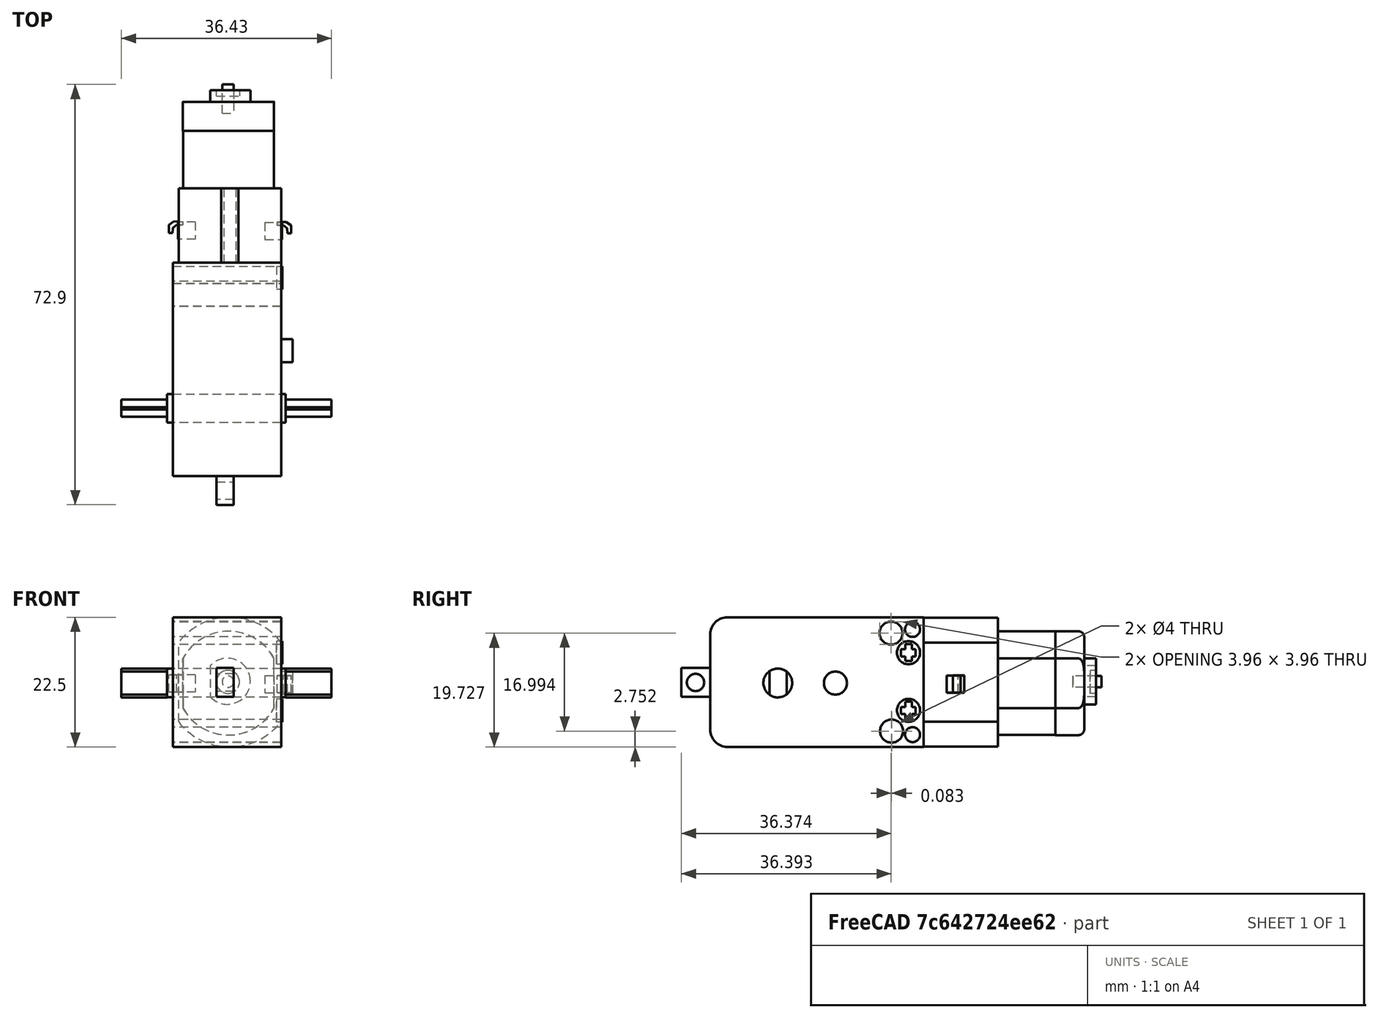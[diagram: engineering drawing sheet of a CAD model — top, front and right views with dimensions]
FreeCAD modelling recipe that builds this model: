
FCSTD DOCUMENT
Label: Motor
objects: Part::Part2DObjectPython×22, Part::Extrusion×22, Part::Cut×9, Part::Feature×4, Part::MultiCommon×3, Part::MultiFuse×3, Part::Fillet×2, App::DocumentObjectGroup×1
note: 65 computed .brp shape members not serialized (recipe doc carries the construction recipe); baked Part::Feature solids carry a one-line shape summary decoded from their .brp

FEATURE [Part::Part2DObjectPython] Circle  # Draft 2D object (typed FeaturePython)
  FirstAngle = 0
  LastAngle = 0
  Placement = pos=(9.4,37,11.25) rot=(0,0.707107,0.707107;3.14159rad)
  Radius = 11.25
FEATURE [Part::Extrusion] Extrude002  label="CaixaMotor"
  Base = -> Circle
  Dir = (0,13,0)
  Solid = false
FEATURE [Part::Part2DObjectPython] Rectangle004  # Draft 2D object (typed FeaturePython)
  FilletRadius = 0
  Height = -22.3491
  Length = 17.8
  Placement = pos=(0.516884,1.09014,22.3973) rot=(1,0,0;1.5708rad)
FEATURE [Part::Extrusion] Extrude008
  Base = -> Rectangle004
  Dir = (0,13,0)
  Placement = pos=(0,36,0) rot=(0,0,1;0rad)
  Solid = false
FEATURE [Part::Part2DObjectPython] Circle002  # Draft 2D object (typed FeaturePython)
  FirstAngle = 0
  LastAngle = 0
  Placement = pos=(59.8722,1.09014,36.5523) rot=(1,0,0;1.5708rad)
  Radius = 4
FEATURE [Part::Part2DObjectPython] Rectangle005  # Draft 2D object (typed FeaturePython)
  FilletRadius = 0
  Height = -8.04493
  Length = -5.41291
  Placement = pos=(56.9026,1.09014,40.4997) rot=(1,0,0;1.5708rad)
FEATURE [Part::Extrusion] Extrude009
  Base = -> Circle002
  Dir = (0,2,0)
  Solid = false
FEATURE [Part::Extrusion] Extrude010
  Base = -> Rectangle005
  Dir = (0,3,0)
  Placement = pos=(0,-0.5,0) rot=(0,0,1;0rad)
  Solid = false
FEATURE [Part::Fillet] Fillet
  Edges = 1 edges r=1: [Edge5]
FEATURE [Part::Part2DObjectPython] Rectangle006  # Draft 2D object (typed FeaturePython)
  FilletRadius = 0
  Height = 20.5
  Length = 15.8
  Placement = pos=(-34.3216,-16.9691,-15.1543) rot=(1,0,0;1.5708rad)
FEATURE [Part::Part2DObjectPython] Circle003  # Draft 2D object (typed FeaturePython)
  FirstAngle = 0
  LastAngle = 0
  Placement = pos=(-26.4216,-16.9691,-4.90432) rot=(1,0,0;1.5708rad)
  Radius = 9
FEATURE [Part::Extrusion] Extrude011
  Base = -> Rectangle006
  Dir = (0,10,0)
  Solid = false
FEATURE [Part::Extrusion] Extrude012
  Base = -> Circle003
  Dir = (0,10,0)
  Solid = false
FEATURE [Part::Part2DObjectPython] Rectangle007  # Draft 2D object (typed FeaturePython)
  FilletRadius = 0
  Height = 5
  Length = 5
  Placement = pos=(0,-19.0704,40.4297) rot=(0.57735,0.57735,0.57735;2.0944rad)
FEATURE [Part::Extrusion] Extrude013
  Base = -> Rectangle007
  Dir = (3,0,0)
  Solid = false
FEATURE [Part::Part2DObjectPython] Circle004  # Draft 2D object (typed FeaturePython)
  FirstAngle = 0
  LastAngle = 0
  Placement = pos=(3,-16.6188,42.8922) rot=(0.57735,0.57735,0.57735;2.0944rad)
  Radius = 1.5
FEATURE [Part::Extrusion] Extrude014
  Base = -> Circle004
  Dir = (5,0,0)
  Placement = pos=(-4,0,0) rot=(0,0,1;0rad)
  Solid = false
FEATURE [Part::Part2DObjectPython] Circle008  # Draft 2D object (typed FeaturePython)
  FirstAngle = 0
  LastAngle = 0
  Placement = pos=(9.57919,64.9001,11.2732) rot=(0,0.707107,0.707107;3.14159rad)
  Radius = 2
FEATURE [Part::Extrusion] Extrude015
  Base = -> Circle008
  Dir = (0,2,0)
  Placement = pos=(0,1,0) rot=(0,0,1;0rad)
  Solid = false
FEATURE [Part::Part2DObjectPython] Circle009  # Draft 2D object (typed FeaturePython)
  FirstAngle = 0
  LastAngle = 0
  Placement = pos=(9.57765,65.9001,11.232) rot=(0,0.707107,0.707107;3.14159rad)
  Radius = 1
FEATURE [Part::Part2DObjectPython] Circle010  # Draft 2D object (typed FeaturePython)
  FirstAngle = 0
  LastAngle = 0
  Placement = pos=(0,-28.9862,26.7464) rot=(0.57735,0.57735,0.57735;2.0944rad)
  Radius = 2
FEATURE [Part::Part2DObjectPython] Circle011  # Draft 2D object (typed FeaturePython)
  FirstAngle = 0
  LastAngle = 0
  Placement = pos=(0,-28.9045,14.2525) rot=(0.57735,0.57735,0.57735;2.0944rad)
  Radius = 2
FEATURE [Part::Extrusion] Extrude017
  Base = -> Circle010
  Dir = (25,0,0)
  Placement = pos=(-2.2,60.36,-7) rot=(0,0,1;0rad)
  Solid = false
FEATURE [Part::Extrusion] Extrude020
  Base = -> Circle011
  Dir = (25,0,0)
  Placement = pos=(-3.2,60.3616,-11.5) rot=(0,0,1;0rad)
  Solid = false
FEATURE [Part::Part2DObjectPython] Circle012  # Draft 2D object (typed FeaturePython)
  FirstAngle = 0
  LastAngle = 0
  Placement = pos=(0,-25.7698,21.2785) rot=(0.57735,0.57735,0.57735;2.0944rad)
  Radius = 1.3
FEATURE [Part::Extrusion] Extrude021
  Base = -> Circle012
  Dir = (25,0,0)
  Placement = pos=(-3.2,60.8663,-0.90035) rot=(0,0,1;0rad)
  Solid = false
FEATURE [Part::Feature] Extrude022
  Placement = pos=(-4.2,60.8663,-19.1548) rot=(0,0,1;0rad)
  shape: bbox 25 x 2.6 x 2.6 mm, 3 faces (baked)
FEATURE [Part::Cut] Cut003
  Tool = -> Extrude022
FEATURE [Part::Cut] Cut004
  Base = -> Cut003
  Tool = -> Extrude017
FEATURE [Part::Cut] Cut005
  Base = -> Cut004
  Tool = -> Extrude020
FEATURE [Part::Part2DObjectPython] DWire  # Draft 2D object (typed FeaturePython)
  Closed = true
  End = (24.1092,43.8585,0)
  FilletRadius = 0
  Start = (24.1092,43.8585,0)
FEATURE [Part::Extrusion] Extrude025
  Base = -> DWire
  Dir = (0,0,3)
  Placement = pos=(-6,0.17,9.39737) rot=(0,0,1;0rad)
  Solid = false
FEATURE [Part::Part2DObjectPython] Rectangle008  # Draft 2D object (typed FeaturePython)
  FilletRadius = 0
  Height = -3
  Length = 2.98
  Placement = pos=(22.53,42.0889,12.3974) rot=(0.57735,0.57735,0.57735;2.0944rad)
FEATURE [Part::Extrusion] Extrude026
  Base = -> Rectangle008
  Dir = (3,0,0)
  Placement = pos=(-6.56795,-1.09,0) rot=(0,0,1;0rad)
  Solid = false
FEATURE [Part::Part2DObjectPython] Circle013  # Draft 2D object (typed FeaturePython)
  FirstAngle = 0
  LastAngle = 0
  Placement = pos=(0,0,30) rot=(0.57735,0.57735,0.57735;2.0944rad)
  Radius = 2.5
FEATURE [Part::Extrusion] Extrude028
  Base = -> Circle013
  Dir = (36.6,0,0)
  Placement = pos=(-9.4,11.74,-20.9117) rot=(0,0,1;0rad)
  Solid = false
FEATURE [Part::Part2DObjectPython] Rectangle009  # Draft 2D object (typed FeaturePython)
  FilletRadius = 0
  Height = 5
  Length = 3
  Placement = pos=(0,0,-30) rot=(0.57735,0.57735,0.57735;2.0944rad)
FEATURE [Part::Extrusion] Extrude029
  Base = -> Rectangle009
  Dir = (8.9,0,0)
  Placement = pos=(-10.37,10.26,36.58) rot=(0,0,1;0rad)
  Solid = false
FEATURE [Part::MultiCommon] Common003
  Placement = pos=(29,0,2) rot=(0,0,1;0rad)
  Shapes = -> [Extrude028,Extrude029]
FEATURE [Part::Feature] Common004
  Placement = pos=(0.5,0,2) rot=(0,0,1;0rad)
  shape: bbox 7.93 x 3 x 4.992 mm, 8 faces (baked)
FEATURE [Part::Part2DObjectPython] Circle014  # Draft 2D object (typed FeaturePython)
  FirstAngle = 0
  LastAngle = 0
  Placement = pos=(18.8,11.7246,11.1008) rot=(0.57735,0.57735,0.57735;2.0944rad)
  Radius = 2.5
FEATURE [Part::Extrusion] Extrude030
  Base = -> Circle014
  Dir = (20.6,0,0)
  Placement = pos=(-19.8,0,0) rot=(0,0,1;0rad)
  Solid = false
FEATURE [Part::MultiFuse] Fusion002  label="EixoRoda0"
  Shapes = -> [Extrude030,Common004]
FEATURE [Part::Part2DObjectPython] Circle015  # Draft 2D object (typed FeaturePython)
  FirstAngle = 0
  LastAngle = 0
  Placement = pos=(18.8,21.72,11.075) rot=(0.57735,-0.57735,-0.57735;2.0944rad)
  Radius = 2
FEATURE [Part::Part2DObjectPython] Circle016  # Draft 2D object (typed FeaturePython)
  FirstAngle = 0
  LastAngle = 0
  Placement = pos=(0,-5.10148,33.3437) rot=(0.57735,0.57735,0.57735;2.0944rad)
  Radius = 2
FEATURE [Part::Extrusion] Extrude032
  Base = -> Circle016
  Dir = (1,0,0)
  Solid = false
FEATURE [Part::Part2DObjectPython] Rectangle010  # Draft 2D object (typed FeaturePython)
  FilletRadius = 0
  Height = -1.2407
  Length = 2.53364
  Placement = pos=(1,-6.39932,33.938) rot=(0.57735,0.57735,0.57735;2.0944rad)
FEATURE [Part::Part2DObjectPython] Rectangle011  # Draft 2D object (typed FeaturePython)
  FilletRadius = 0
  Height = -2.95156
  Length = 1.16234
  Placement = pos=(1,-5.6549,34.8391) rot=(0.57735,0.57735,0.57735;2.0944rad)
FEATURE [Part::Extrusion] Extrude033
  Base = -> Rectangle010
  Dir = (0.5,0,0)
  Placement = pos=(-0.2,0,0) rot=(0,0,1;0rad)
  Solid = false
FEATURE [Part::Extrusion] Extrude034
  Base = -> Rectangle011
  Dir = (0.5,0,0)
  Placement = pos=(-0.2,0,0) rot=(0,0,1;0rad)
  Solid = false
FEATURE [Part::Cut] Cut007
  Base = -> Extrude032
  Tool = -> Extrude033
FEATURE [Part::Feature] Part__Mirroring002  label="Alca2"
  Placement = pos=(-0.7,0.51,12.5) rot=(0,0,1;0rad)
  shape: bbox 4.572 x 3.074 x 3 mm, 16 faces (baked)
FEATURE [Part::Feature] Cut009  label="Parafuso002"
  Placement = pos=(18,39.5,-27) rot=(0,0,1;0rad)
  shape: bbox 1 x 4 x 4 mm, 20 faces (baked)
FEATURE [Part::Fillet] Fillet002  label="ParteMotor1"
  Base = -> Fillet
  Edges = 1 edges r=1: [Edge3]
  Placement = pos=(-0.226159,9.98502,-0.2) rot=(0,0,1;0rad)
FEATURE [Part::MultiCommon] Common  label="BooleanCaixaMotor"
  Placement = pos=(0.5,-0.1,0) rot=(0,0,1;0rad)
  Shapes = -> [Extrude008,Extrude002]
FEATURE [Part::Cut] Cut  label="SuporteEixo"
  Base = -> Extrude009
  Placement = pos=(-50.3996,63.81,-25.1656) rot=(0,0,1;0rad)
  Tool = -> Extrude010
FEATURE [Part::Cut] Cut002  label="ParteMotor2"
  Base = -> Cut
  Tool = -> Extrude015
FEATURE [Part::Extrusion] Extrude016  label="EixoMotor"
  Base = -> Circle009
  Dir = (0,5,0)
  Placement = pos=(-0.00220966,-3,0.0854275) rot=(0,0,1;0rad)
  Solid = false
FEATURE [Part::MultiCommon] Common002  label="CorpoMotor"
  Placement = pos=(36.1062,66.8259,15.9674) rot=(0,0,1;0rad)
  Shapes = -> [Extrude011,Extrude012]
FEATURE [Part::Cut] Cut001  label="Prendedor"
  Base = -> Extrude013
  Placement = pos=(7.59052,14.07,-31.7158) rot=(0,0,1;0rad)
  Tool = -> Extrude014
FEATURE [Part::Cut] Cut006  label="CaxiaFurada"
  Base = -> Cut005
  Tool = -> Extrude021
FEATURE [Part::MultiFuse] Fusion001  label="Alca1"
  Shapes = -> [Extrude025,Extrude026]
FEATURE [Part::MultiFuse] Fusion003  label="EixoRoda"
  Shapes = -> [Fusion002,Common003]
FEATURE [Part::Extrusion] Extrude031  label="Pino"
  Base = -> Circle015
  Dir = (2,0,0)
  Solid = false
FEATURE [Part::Cut] Cut008  label="Parafuso1"
  Base = -> Cut007
  Placement = pos=(18,39.5,-17) rot=(0,0,1;0rad)
  Tool = -> Extrude034
FEATURE [App::DocumentObjectGroup] Grupo  label="Motor1"
  Group = -> [Common,Cut,Common002,Fillet002,Cut001,Cut002,Extrude016,Cut006,Fusion001,Fusion003,Extrude031,Cut008,Cut009,Part__Mirroring002]
